# Revit family: Electrical-Box_Accessory_FSR_FL-GRD-PourPan
name_source: partatom
category: Generic Models
units: mm (PartAtom-declared; Revit-internal decimal feet)

## family parameters
Can host rebar = No
Classification Number = 23.80.50.00
Cut with Voids When Loaded = No
Host = Face
Maintain Annotation Orientation = No
Part Type = Normal
Room Calculation Point = No
Round Connector Dimension = Use Diameter
Shared = No

## types (1)
- FL-GRD200
    Assembly Code = D5020100
    Construction Details = http://www.arcat.com
    Cost = 0 $
    Default Elevation = 0' - 0"
    Description = FSR Concrete Floor Box Pour Pan - FL-GRD200
    Expected Lifespan (Years) = 0
    Green Building-LEED = http://www.arcat.com
    Installation-Fabrication = ftp://doclib.fsrinc.com/
    Keynote = 26 27 26
    Maintenance Schedule (Months) = 0
    Manufacturer = FSR, Inc
    Manufacturer Fax = 973-785-4207
    Manufacturer Website = http://fsrinc.com
    Model = FL-GRD200
    Product Data = http://www.arcat.com
    Revision = R1_2016-06
    Sales Information = http://fsrinc.com
    Specification = http://www.arcat.com
    Standards Conformance = as Specified
    Test Data = ftp://doclib.fsrinc.com/
    URL = http://fsrinc.com
    Unit Depth = 0' - 2 1/16"
    Unit Height = 1' - 3 3/4"
    Unit Width = 1' - 3 3/4"
    Warranty Duration (Years) = 0

## geometry (parser evidence)
native form markers: Sweep x2
no freeform markers — native parametric forms only
